# Revit family: IglooPro Round Shower
name_source: partatom
category: Generic Models
units: mm (PartAtom-declared; Revit-internal decimal feet)

## family parameters
Always vertical = Yes
Can host rebar = No
Cut with Voids When Loaded = No
Part Type = Normal
Room Calculation Point = No
Round Connector Dimension = Use Diameter
Shared = No
Work Plane-Based = No

## types (16) — shared parameters
Description = Shower corner
ETIM class = EC010038
Glass Type = Glass Clear
Manufacturer = Hafa Bathroom Group
Profile and Handle material = Aluminium
URL = https://www.hafa.se

## per-type parameters (varying)
| type | Diagonal | Doorblade length | Doorblade width | Length | Placement handle L | Placement handle W | Ref plane hor | Straight part of door l | Straight part of door w | Width |
| 1450401 IglooPro Round 90x90 Clear | 924 mm | 695 mm | 695 mm | 900 mm  [stored 2.95276 ft] | 311 mm | 297 mm | 301 mm | 400 mm  [stored 1.31234 ft] | 400 mm  [stored 1.31234 ft] | 900 mm  [stored 2.95276 ft] |
| 1450400 IglooPro Round 80x80 Clear | 986 mm | 595 mm  [stored 1.9521 ft] | 595 mm  [stored 1.9521 ft] | 800 mm  [stored 2.62467 ft] | 311 mm | 297 mm | 201 mm  [stored 0.659449 ft] | 300 mm | 300 mm | 800 mm  [stored 2.62467 ft] |
| 1450420 IglooPro Round 70x70 Clear | 924 mm | 495 mm | 495 mm | 700 mm  [stored 2.29659 ft] | 311 mm | 297 mm | 101 mm | 200 mm  [stored 0.656168 ft] | 200 mm  [stored 0.656168 ft] | 700 mm  [stored 2.29659 ft] |
| 1450421 IglooPro Round 70x80 Clear | 924 mm | 495 mm | 595 mm  [stored 1.9521 ft] | 700 mm  [stored 2.29659 ft] | 311 mm | 284 mm | 101 mm | 200 mm  [stored 0.656168 ft] | 300 mm | 800 mm  [stored 2.62467 ft] |
| 1450421 IglooPro Round 80x70 Clear | 924 mm | 595 mm  [stored 1.9521 ft] | 495 mm | 800 mm  [stored 2.62467 ft] | 284 mm | 310 mm | 201 mm  [stored 0.659449 ft] | 300 mm | 200 mm  [stored 0.656168 ft] | 700 mm  [stored 2.29659 ft] |
| 1450422 IglooPro Round 70x90 Clear | 924 mm | 724 mm | 495 mm | 929 mm | 269 mm  [stored 0.882546 ft] | 325 mm | 330 mm | 429 mm | 200 mm  [stored 0.656168 ft] | 700 mm  [stored 2.29659 ft] |
| 1450422 IglooPro Round 90x70 Clear | 924 mm | 495 mm | 695 mm | 700 mm  [stored 2.29659 ft] | 322 mm | 272 mm | 101 mm | 200 mm  [stored 0.656168 ft] | 400 mm  [stored 1.31234 ft] | 900 mm  [stored 2.95276 ft] |
| 1450423 IglooPro Round 70x100 Clear | 924 mm | 495 mm | 795 mm | 700 mm  [stored 2.29659 ft] | 333 mm | 260 mm | 101 mm | 200 mm  [stored 0.656168 ft] | 500 mm  [stored 1.64042 ft] | 1000 mm |
| 1450423 IglooPro Round 100x70 Clear | 924 mm | 795 mm | 495 mm | 1000 mm | 251 mm | 332 mm | 401 mm | 500 mm  [stored 1.64042 ft] | 200 mm  [stored 0.656168 ft] | 700 mm  [stored 2.29659 ft] |
| 1450424 IglooPro Round 80x90 Clear | 924 mm | 595 mm  [stored 1.9521 ft] | 695 mm | 800 mm  [stored 2.62467 ft] | 311 mm | 285 mm | 201 mm  [stored 0.659449 ft] | 300 mm | 400 mm  [stored 1.31234 ft] | 900 mm  [stored 2.95276 ft] |
| 1450424 IglooPro Round 90x80 Clear | 924 mm | 695 mm | 595 mm  [stored 1.9521 ft] | 900 mm  [stored 2.95276 ft] | 285 mm | 309 mm  [stored 1.01378 ft] | 301 mm | 400 mm  [stored 1.31234 ft] | 300 mm | 800 mm  [stored 2.62467 ft] |
| 1450425 IglooPro Round 80x100 Clear | 924 mm | 595 mm  [stored 1.9521 ft] | 795 mm | 800 mm  [stored 2.62467 ft] | 320 mm | 274 mm | 201 mm  [stored 0.659449 ft] | 300 mm | 500 mm  [stored 1.64042 ft] | 1000 mm |
| 1450425 IglooPro Round 100x80 Clear | 924 mm | 795 mm | 595 mm  [stored 1.9521 ft] | 1000 mm | 273 mm | 319 mm | 401 mm | 500 mm  [stored 1.64042 ft] | 300 mm | 800 mm  [stored 2.62467 ft] |
| 1450426 IglooPro Round 90x100 Clear | 924 mm | 695 mm | 795 mm | 900 mm  [stored 2.95276 ft] | 311 mm | 286 mm | 301 mm | 400 mm  [stored 1.31234 ft] | 500 mm  [stored 1.64042 ft] | 1000 mm |
| 1450426 IglooPro Round 100x90 Clear | 924 mm | 795 mm | 695 mm | 1000 mm | 287 mm | 308 mm | 401 mm | 500 mm  [stored 1.64042 ft] | 400 mm  [stored 1.31234 ft] | 900 mm  [stored 2.95276 ft] |
| 1450427 IglooPro Round 100x100 Clear | 924 mm | 795 mm | 795 mm | 1000 mm | 297 mm | 297 mm | 401 mm | 500 mm  [stored 1.64042 ft] | 500 mm  [stored 1.64042 ft] | 1000 mm |

note: [stored X ft] marks values corroborated as IEEE doubles in the binary element streams (Revit-internal decimal feet)

## geometry (parser evidence)
native form markers: Sweep x8
no freeform markers — native parametric forms only
